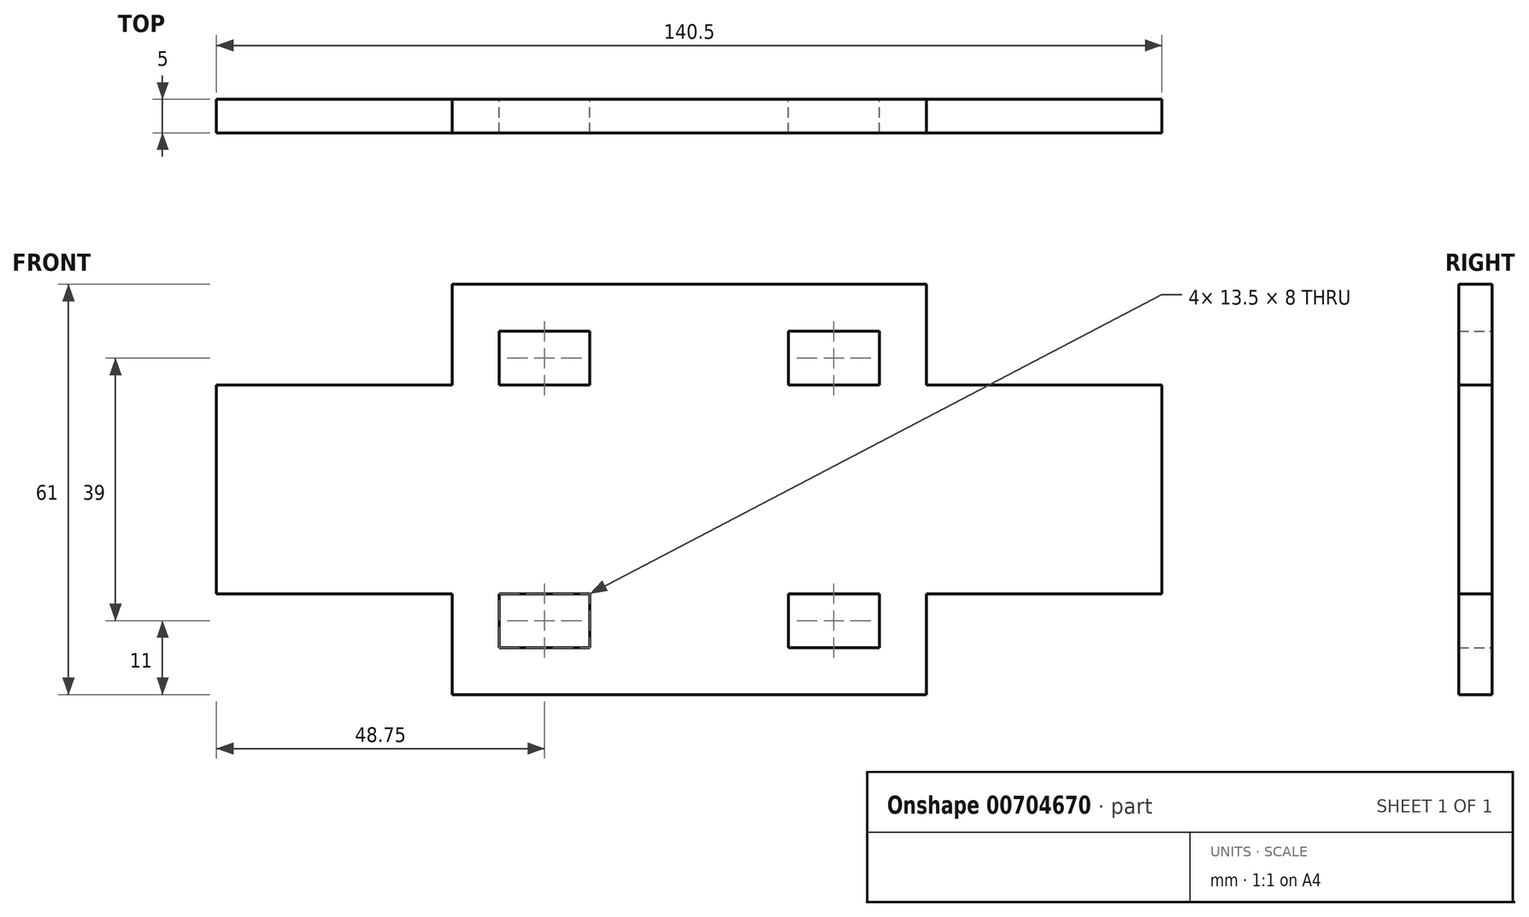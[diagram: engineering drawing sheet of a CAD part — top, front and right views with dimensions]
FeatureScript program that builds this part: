
annotation { "Feature Type Name" : "Feature", "Feature Type Description" : "" }
export const myFeature = defineFeature(function(context is Context, id is Id, definition is map)
    precondition{}
    {
        {
            var Q0;
            Q0=qCreatedBy(makeId("Front.planeOp"),FACE);
            var sketch = newSketch(context, id + "F0", { "sketchPlane" : qUnion([Q0])});
            skLineSegment(sketch, "E0.bottom", {"start": v(-35.25, 30.5) * mm, "end": v(35.25, 30.5) * mm});
            skLineSegment(sketch, "E0.top", {"start": v(-35.25, -30.5) * mm, "end": v(35.25, -30.5) * mm});
            skLineSegment(sketch, "E0.left", {"start": v(-35.25, 30.5) * mm, "end": v(-35.25, -30.5) * mm});
            skLineSegment(sketch, "E0.right", {"start": v(35.25, 30.5) * mm, "end": v(35.25, -30.5) * mm});
            skPoint(sketch, "E0.middle", {"position": v(0, 0) * mm});
            skLineSegment(sketch, "E1.bottom", {"start": v(-28.25, 23.5) * mm, "end": v(-14.75, 23.5) * mm});
            skLineSegment(sketch, "E1.top", {"start": v(-28.25, 15.5) * mm, "end": v(-14.75, 15.5) * mm});
            skLineSegment(sketch, "E1.left", {"start": v(-28.25, 23.5) * mm, "end": v(-28.25, 15.5) * mm});
            skLineSegment(sketch, "E1.right", {"start": v(-14.75, 23.5) * mm, "end": v(-14.75, 15.5) * mm});
            skLineSegment(sketch, "E2.bottom", {"start": v(14.75, 23.5) * mm, "end": v(28.25, 23.5) * mm});
            skLineSegment(sketch, "E2.top", {"start": v(14.75, 15.5) * mm, "end": v(28.25, 15.5) * mm});
            skLineSegment(sketch, "E2.left", {"start": v(14.75, 23.5) * mm, "end": v(14.75, 15.5) * mm});
            skLineSegment(sketch, "E2.right", {"start": v(28.25, 23.5) * mm, "end": v(28.25, 15.5) * mm});
            skLineSegment(sketch, "E3.bottom", {"start": v(14.75, -15.5) * mm, "end": v(28.25, -15.5) * mm});
            skLineSegment(sketch, "E3.top", {"start": v(14.75, -23.5) * mm, "end": v(28.25, -23.5) * mm});
            skLineSegment(sketch, "E3.left", {"start": v(14.75, -15.5) * mm, "end": v(14.75, -23.5) * mm});
            skLineSegment(sketch, "E3.right", {"start": v(28.25, -15.5) * mm, "end": v(28.25, -23.5) * mm});
            skLineSegment(sketch, "E4.bottom", {"start": v(-28.25, -15.5) * mm, "end": v(-14.75, -15.5) * mm});
            skLineSegment(sketch, "E4.top", {"start": v(-28.25, -23.5) * mm, "end": v(-14.75, -23.5) * mm});
            skLineSegment(sketch, "E4.left", {"start": v(-28.25, -15.5) * mm, "end": v(-28.25, -23.5) * mm});
            skLineSegment(sketch, "E4.right", {"start": v(-14.75, -15.5) * mm, "end": v(-14.75, -23.5) * mm});
            skLineSegment(sketch, "E5.bottom", {"start": v(-14.75, 30.5) * mm, "end": v(14.75, 30.5) * mm});
            skLineSegment(sketch, "E5.top", {"start": v(-14.75, 65.5) * mm, "end": v(14.75, 65.5) * mm});
            skLineSegment(sketch, "E5.left", {"start": v(-14.75, 30.5) * mm, "end": v(-14.75, 65.5) * mm});
            skLineSegment(sketch, "E5.right", {"start": v(14.75, 30.5) * mm, "end": v(14.75, 65.5) * mm});
            skLineSegment(sketch, "E6.MirrorCS", {"start": v(-14.75, -30.5) * mm, "end": v(14.75, -30.5) * mm});
            skLineSegment(sketch, "E7.MirrorCS", {"start": v(-14.75, -30.5) * mm, "end": v(-14.75, -65.5) * mm});
            skLineSegment(sketch, "E8.MirrorCS", {"start": v(14.75, -30.5) * mm, "end": v(14.75, -65.5) * mm});
            skLineSegment(sketch, "E9.MirrorCS", {"start": v(-14.75, -65.5) * mm, "end": v(14.75, -65.5) * mm});
            skLineSegment(sketch, "E10.bottom", {"start": v(35.25, 15.5) * mm, "end": v(70.25, 15.5) * mm});
            skLineSegment(sketch, "E10.top", {"start": v(35.25, -15.5) * mm, "end": v(70.25, -15.5) * mm});
            skLineSegment(sketch, "E10.left", {"start": v(35.25, 15.5) * mm, "end": v(35.25, -15.5) * mm});
            skLineSegment(sketch, "E10.right", {"start": v(70.25, 15.5) * mm, "end": v(70.25, -15.5) * mm});
            skLineSegment(sketch, "E11.MirrorCS", {"start": v(-70.25, 15.5) * mm, "end": v(-70.25, -15.5) * mm});
            skLineSegment(sketch, "E12.MirrorCS", {"start": v(-35.25, 15.5) * mm, "end": v(-35.25, -15.5) * mm});
            skLineSegment(sketch, "E13.MirrorCS", {"start": v(-35.25, -15.5) * mm, "end": v(-70.25, -15.5) * mm});
            skLineSegment(sketch, "E14.MirrorCS", {"start": v(-35.25, 15.5) * mm, "end": v(-70.25, 15.5) * mm});
            skSolve(sketch);
        }
        {
            var Q0;
            Q0=makeQuery(id+"F0.imprint","IMPRINT",FACE,{"disambiguationData":[TD([[makeQuery(id+"F0.imprint","IMPRINT",EDGE,{"derivedFrom":sQuery(id+"F0.wireOp",EDGE,"E11.MirrorCS")}),1.0]])]});
            var Q1;
            Q1=makeQuery(id+"F0.imprint","IMPRINT",FACE,{"disambiguationData":[TD([[makeQuery(id+"F0.imprint","IMPRINT",EDGE,{"derivedFrom":sQuery(id+"F0.wireOp",EDGE,"E1.bottom")}),1.0]])]});
            var Q2;
            Q2=makeQuery(id+"F0.imprint","IMPRINT",FACE,{"disambiguationData":[TD([[makeQuery(id+"F0.imprint","IMPRINT",EDGE,{"derivedFrom":sQuery(id+"F0.wireOp",EDGE,"E5.bottom")}),1.0]])]});
            var Q3;
            Q3=makeQuery(id+"F0.imprint","IMPRINT",FACE,{"disambiguationData":[TD([[makeQuery(id+"F0.imprint","IMPRINT",EDGE,{"derivedFrom":sQuery(id+"F0.wireOp",EDGE,"E6.MirrorCS")}),-1.0]])]});
            var Q4;
            Q4=makeQuery(id+"F0.imprint","IMPRINT",FACE,{"disambiguationData":[TD([[makeQuery(id+"F0.imprint","IMPRINT",EDGE,{"derivedFrom":sQuery(id+"F0.wireOp",EDGE,"E10.bottom")}),-1.0]])]});
            extrude(context, id + "F1", {"entities" : qUnion([Q0, Q1, Q2, Q3, Q4]), "depth" : 5 * mm, "offsetDistance" : 25 * mm});
        }
    });
